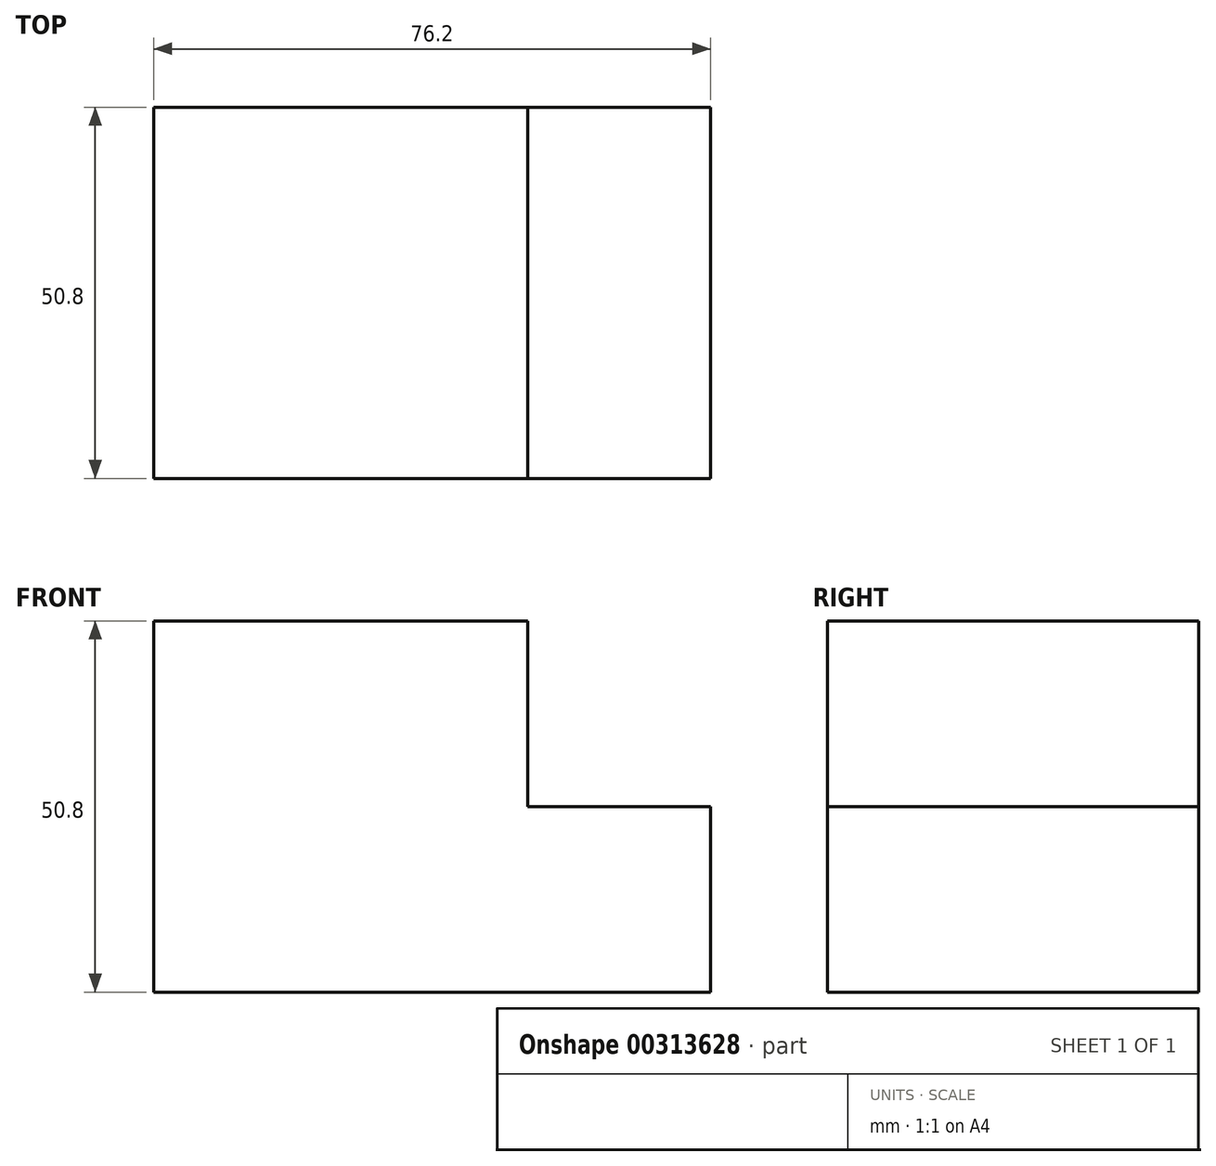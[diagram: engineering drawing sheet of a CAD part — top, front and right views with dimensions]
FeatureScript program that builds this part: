
annotation { "Feature Type Name" : "Feature", "Feature Type Description" : "" }
export const myFeature = defineFeature(function(context is Context, id is Id, definition is map)
    precondition{}
    {
        {
            var Q0;
            Q0=qCreatedBy(makeId("Front.planeOp"),FACE);
            var sketch = newSketch(context, id + "F0", { "sketchPlane" : qUnion([Q0])});
            skLineSegment(sketch, "E0", {"start": v(-32.4, -28.89) * mm, "end": v(43.8, -28.89) * mm});
            skLineSegment(sketch, "E1", {"start": v(43.8, -28.89) * mm, "end": v(43.8, -3.49) * mm});
            skLineSegment(sketch, "E2", {"start": v(43.8, -3.49) * mm, "end": v(18.78, -3.49) * mm});
            skLineSegment(sketch, "E3", {"start": v(18.78, -3.49) * mm, "end": v(18.78, 21.91) * mm});
            skLineSegment(sketch, "E4", {"start": v(18.78, 21.91) * mm, "end": v(-32.4, 21.91) * mm});
            skLineSegment(sketch, "E5", {"start": v(-32.4, 21.91) * mm, "end": v(-32.4, -28.89) * mm});
            skSolve(sketch);
        }
        {
            var Q0;
            Q0=makeQuery(id+"F0.imprint","IMPRINT",FACE,{"disambiguationData":[TD([[makeQuery(id+"F0.imprint","IMPRINT",EDGE,{"derivedFrom":sQuery(id+"F0.wireOp",EDGE,"E0")}),1.0]])]});
            extrude(context, id + "F1", {"entities" : qUnion([Q0]), "depth" : 50.8 * mm});
        }
    });
